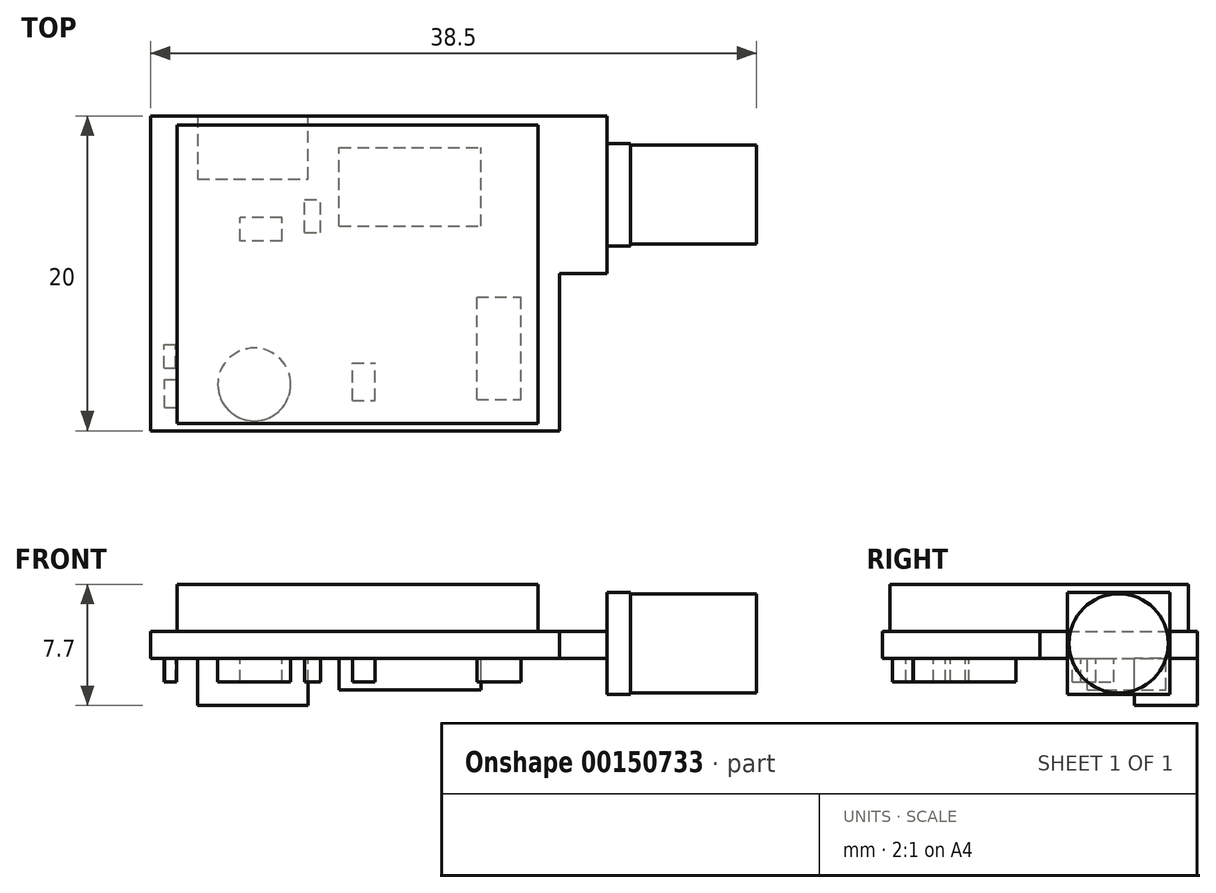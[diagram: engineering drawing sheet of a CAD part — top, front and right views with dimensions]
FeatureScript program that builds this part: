
annotation { "Feature Type Name" : "Feature", "Feature Type Description" : "" }
export const myFeature = defineFeature(function(context is Context, id is Id, definition is map)
    precondition{}
    {
        {
            var Q0;
            Q0=qCreatedBy(makeId("Top.planeOp"),FACE);
            var sketch = newSketch(context, id + "F0", { "sketchPlane" : qUnion([Q0])});
            skLineSegment(sketch, "E0.top", {"start": v(-26, 0) * mm, "end": v(0, 0) * mm});
            skLineSegment(sketch, "E0.left", {"start": v(-26, 20) * mm, "end": v(-26, 0) * mm});
            skLineSegment(sketch, "E1", {"start": v(0, 10) * mm, "end": v(3, 10) * mm});
            skLineSegment(sketch, "E2", {"start": v(3, 10) * mm, "end": v(3, 20) * mm});
            skLineSegment(sketch, "E3", {"start": v(0, 0) * mm, "end": v(0, 10) * mm});
            skLineSegment(sketch, "E4", {"start": v(3, 20) * mm, "end": v(-26, 20) * mm});
            skSolve(sketch);
        }
        {
            var Q0;
            Q0=makeQuery(id+"F0.imprint","IMPRINT",FACE,{"disambiguationData":[TD([[makeQuery(id+"F0.imprint","IMPRINT",EDGE,{"derivedFrom":sQuery(id+"F0.wireOp",EDGE,"E0.top")}),1.0]])]});
            extrude(context, id + "F1", {"entities" : qUnion([Q0]), "depth" : 1.7 * mm});
        }
        {
            var Q0;
            Q0=makeQuery(id+"F1.opExtrude","CAP_FACE",FACE,{"disambiguationData":[OSD([sQuery(id+"F0.wireOp",EDGE,"E0.top"),sQuery(id+"F0.wireOp",EDGE,"E0.left"),sQuery(id+"F0.wireOp",EDGE,"E1"),sQuery(id+"F0.wireOp",EDGE,"E2"),sQuery(id+"F0.wireOp",EDGE,"E3"),sQuery(id+"F0.wireOp",EDGE,"E4")])],"isStart":false});
            var sketch = newSketch(context, id + "F2", { "sketchPlane" : qUnion([Q0])});
            skLineSegment(sketch, "E5.bottom", {"start": v(-24.3, 19.42) * mm, "end": v(-1.39, 19.42) * mm});
            skLineSegment(sketch, "E5.top", {"start": v(-24.3, 0.48) * mm, "end": v(-1.39, 0.48) * mm});
            skLineSegment(sketch, "E5.left", {"start": v(-24.3, 19.42) * mm, "end": v(-24.3, 0.48) * mm});
            skLineSegment(sketch, "E5.right", {"start": v(-1.39, 19.42) * mm, "end": v(-1.39, 0.48) * mm});
            skSolve(sketch);
        }
        {
            var Q0;
            Q0=makeQuery(id+"F2.imprint","IMPRINT",FACE,{"disambiguationData":[TD([[makeQuery(id+"F2.imprint","IMPRINT",EDGE,{"derivedFrom":sQuery(id+"F2.wireOp",EDGE,"E5.bottom")}),-1.0]])]});
            extrude(context, id + "F3", {"entities" : qUnion([Q0]), "operationType" : NewBodyOperationType.ADD, "depth" : 3 * mm});
        }
        {
            var Q0;
            Q0=makeQuery(id+"F1.opExtrude","CAP_FACE",FACE,{"disambiguationData":[OSD([sQuery(id+"F0.wireOp",EDGE,"E0.top"),sQuery(id+"F0.wireOp",EDGE,"E0.left"),sQuery(id+"F0.wireOp",EDGE,"E1"),sQuery(id+"F0.wireOp",EDGE,"E2"),sQuery(id+"F0.wireOp",EDGE,"E3"),sQuery(id+"F0.wireOp",EDGE,"E4")])],"isStart":true});
            var sketch = newSketch(context, id + "F4", { "sketchPlane" : qUnion([Q0])});
            skLineSegment(sketch, "E6.bottom", {"start": v(-14, -13) * mm, "end": v(-5, -13) * mm});
            skLineSegment(sketch, "E6.top", {"start": v(-14, -18) * mm, "end": v(-5, -18) * mm});
            skLineSegment(sketch, "E6.left", {"start": v(-14, -13) * mm, "end": v(-14, -18) * mm});
            skLineSegment(sketch, "E6.right", {"start": v(-5, -13) * mm, "end": v(-5, -18) * mm});
            skSolve(sketch);
        }
        {
            var Q0;
            Q0=makeQuery(id+"F4.imprint","IMPRINT",FACE,{"disambiguationData":[TD([[makeQuery(id+"F4.imprint","IMPRINT",EDGE,{"derivedFrom":sQuery(id+"F4.wireOp",EDGE,"E6.bottom")}),-1.0]])]});
            extrude(context, id + "F5", {"entities" : qUnion([Q0]), "operationType" : NewBodyOperationType.ADD, "depth" : 2 * mm});
        }
        {
            var Q0;
            Q0=makeQuery(id+"F1.opExtrude","CAP_FACE",FACE,{"disambiguationData":[OSD([sQuery(id+"F0.wireOp",EDGE,"E0.top"),sQuery(id+"F0.wireOp",EDGE,"E0.left"),sQuery(id+"F0.wireOp",EDGE,"E1"),sQuery(id+"F0.wireOp",EDGE,"E2"),sQuery(id+"F0.wireOp",EDGE,"E3"),sQuery(id+"F0.wireOp",EDGE,"E4")])],"isStart":true});
            var sketch = newSketch(context, id + "F6", { "sketchPlane" : qUnion([Q0])});
            skLineSegment(sketch, "E7.bottom", {"start": v(-5.27, -1.98) * mm, "end": v(-2.46, -1.98) * mm});
            skLineSegment(sketch, "E7.top", {"start": v(-5.27, -8.48) * mm, "end": v(-2.46, -8.48) * mm});
            skLineSegment(sketch, "E7.left", {"start": v(-5.27, -1.98) * mm, "end": v(-5.27, -8.48) * mm});
            skLineSegment(sketch, "E7.right", {"start": v(-2.46, -1.98) * mm, "end": v(-2.46, -8.48) * mm});
            skLineSegment(sketch, "E8.bottom", {"start": v(-16.2, -12.6) * mm, "end": v(-15.2, -12.6) * mm});
            skLineSegment(sketch, "E8.top", {"start": v(-16.2, -14.68) * mm, "end": v(-15.2, -14.68) * mm});
            skLineSegment(sketch, "E8.left", {"start": v(-16.2, -12.6) * mm, "end": v(-16.2, -14.68) * mm});
            skLineSegment(sketch, "E8.right", {"start": v(-15.2, -12.6) * mm, "end": v(-15.2, -14.68) * mm});
            skLineSegment(sketch, "E9.bottom", {"start": v(-17.65, -12.06) * mm, "end": v(-20.3, -12.06) * mm});
            skLineSegment(sketch, "E9.top", {"start": v(-17.65, -13.54) * mm, "end": v(-20.3, -13.54) * mm});
            skLineSegment(sketch, "E9.left", {"start": v(-17.65, -12.06) * mm, "end": v(-17.65, -13.54) * mm});
            skLineSegment(sketch, "E9.right", {"start": v(-20.3, -12.06) * mm, "end": v(-20.3, -13.54) * mm});
            skLineSegment(sketch, "E10.bottom", {"start": v(-13.16, -1.93) * mm, "end": v(-11.72, -1.93) * mm});
            skLineSegment(sketch, "E10.top", {"start": v(-13.16, -4.32) * mm, "end": v(-11.72, -4.32) * mm});
            skLineSegment(sketch, "E10.left", {"start": v(-13.16, -1.93) * mm, "end": v(-13.16, -4.32) * mm});
            skLineSegment(sketch, "E10.right", {"start": v(-11.72, -1.93) * mm, "end": v(-11.72, -4.32) * mm});
            skLineSegment(sketch, "E11.bottom", {"start": v(-25.08, -1.5) * mm, "end": v(-24.34, -1.5) * mm});
            skLineSegment(sketch, "E11.top", {"start": v(-25.08, -3.25) * mm, "end": v(-24.34, -3.25) * mm});
            skLineSegment(sketch, "E11.left", {"start": v(-25.08, -1.5) * mm, "end": v(-25.08, -3.25) * mm});
            skLineSegment(sketch, "E11.right", {"start": v(-24.34, -1.5) * mm, "end": v(-24.34, -3.25) * mm});
            skLineSegment(sketch, "E12.bottom", {"start": v(-25.14, -4) * mm, "end": v(-24.4, -4) * mm});
            skLineSegment(sketch, "E12.top", {"start": v(-25.14, -5.5) * mm, "end": v(-24.4, -5.5) * mm});
            skLineSegment(sketch, "E12.left", {"start": v(-25.14, -4) * mm, "end": v(-25.14, -5.5) * mm});
            skLineSegment(sketch, "E12.right", {"start": v(-24.4, -4) * mm, "end": v(-24.4, -5.5) * mm});
            skCircle(sketch, "E13", {"center": v(-19.4, -2.94) * mm, "radius": 2.31 * mm});
            skSolve(sketch);
        }
        {
            var Q0;
            Q0 = qSketchRegion(id + "F6", true);
            extrude(context, id + "F7", {"entities" : qUnion([Q0]), "operationType" : NewBodyOperationType.ADD, "depth" : 1.5 * mm});
        }
        {
            var Q0;
            Q0=makeQuery(id+"F1.opExtrude","CAP_FACE",FACE,{"disambiguationData":[OSD([sQuery(id+"F0.wireOp",EDGE,"E0.top"),sQuery(id+"F0.wireOp",EDGE,"E0.left"),sQuery(id+"F0.wireOp",EDGE,"E1"),sQuery(id+"F0.wireOp",EDGE,"E2"),sQuery(id+"F0.wireOp",EDGE,"E3"),sQuery(id+"F0.wireOp",EDGE,"E4")])],"isStart":true});
            var sketch = newSketch(context, id + "F8", { "sketchPlane" : qUnion([Q0])});
            skLineSegment(sketch, "E14", {"start": v(-23, -20) * mm, "end": v(-23, -16) * mm});
            skLineSegment(sketch, "E15", {"start": v(-23, -16) * mm, "end": v(-16, -16) * mm});
            skLineSegment(sketch, "E16", {"start": v(-16, -16) * mm, "end": v(-16, -20) * mm});
            skSolve(sketch);
        }
        {
            var Q0;
            {var subQ0=sQuery(id+"F8.wireOp",EDGE,"E14");Q0=makeQuery(id+"F8.imprint","IMPRINT",FACE,{"disambiguationData":[TD([[makeQuery(id+"F8.imprint","IMPRINT",EDGE,{"derivedFrom":subQ0}),-1.0]])]});}
            extrude(context, id + "F9", {"entities" : qUnion([Q0]), "operationType" : NewBodyOperationType.ADD, "depth" : 3 * mm});
        }
        {
            var Q0;
            Q0=makeQuery(id+"F1.opExtrude","SWEPT_FACE",FACE,{"disambiguationData":[OSD([sQuery(id+"F0.wireOp",EDGE,"E2")])]});
            var sketch = newSketch(context, id + "F10", { "sketchPlane" : qUnion([Q0])});
            skLineSegment(sketch, "E17.bottom", {"start": v(18.25, -2.3) * mm, "end": v(11.75, -2.3) * mm});
            skLineSegment(sketch, "E17.top", {"start": v(18.25, 4.2) * mm, "end": v(11.75, 4.2) * mm});
            skLineSegment(sketch, "E17.left", {"start": v(18.25, -2.3) * mm, "end": v(18.25, 4.2) * mm});
            skLineSegment(sketch, "E17.right", {"start": v(11.75, -2.3) * mm, "end": v(11.75, 4.2) * mm});
            skSolve(sketch);
        }
        {
            var Q0;
            {var subQ0=sQuery(id+"F10.wireOp",EDGE,"E17.bottom");Q0=makeQuery(id+"F10.imprint","IMPRINT",FACE,{"disambiguationData":[TD([[makeQuery(id+"F10.imprint","IMPRINT",EDGE,{"derivedFrom":subQ0}),-1.0]])]});}
            var Q1;
            {var subQ0=sQuery(id+"F10.wireOp",EDGE,"E17.left");var subQ1=sQuery(id+"F0.wireOp",EDGE,"E2");var subQ2=makeQuery(id+"F1.opExtrude","CAP_EDGE",EDGE,{"disambiguationData":[OSD([subQ1])],"isStart":true});var subQ3=makeQuery(id+"F10.imprint","INTERSECT",VERTEX,{"derivedFrom":[subQ2,subQ0]});Q1=makeQuery(id+"F10.imprint","IMPRINT",FACE,{"disambiguationData":[TD([[makeQuery(id+"F10.imprint","IMPRINT",EDGE,{"disambiguationData":[TD([[subQ3,-1.0]])],"derivedFrom":subQ0}),1.0]])]});}
            var Q2;
            {var subQ0=sQuery(id+"F10.wireOp",EDGE,"E17.top");Q2=makeQuery(id+"F10.imprint","IMPRINT",FACE,{"disambiguationData":[TD([[makeQuery(id+"F10.imprint","IMPRINT",EDGE,{"derivedFrom":subQ0}),1.0]])]});}
            extrude(context, id + "F11", {"entities" : qUnion([Q0, Q1, Q2]), "operationType" : NewBodyOperationType.ADD, "depth" : 1.5 * mm});
        }
        {
            var Q0;
            Q0=makeQuery(id+"F11.opExtrude","CAP_FACE",FACE,{"disambiguationData":[OSD([sQuery(id+"F10.wireOp",EDGE,"E17.bottom"),sQuery(id+"F10.wireOp",EDGE,"E17.top"),sQuery(id+"F10.wireOp",EDGE,"E17.left"),sQuery(id+"F10.wireOp",EDGE,"E17.right")])],"isStart":false});
            var sketch = newSketch(context, id + "F12", { "sketchPlane" : qUnion([Q0])});
            skCircle(sketch, "E18", {"center": v(15, 0.95) * mm, "radius": 3.15 * mm});
            skPoint(sketch, "E18.centerSnap0", {"position": v(15, -2.3) * mm});
            skPoint(sketch, "E18.centerSnap1", {"position": v(18.25, 0.95) * mm});
            skSolve(sketch);
        }
        {
            var Q0;
            Q0=makeQuery(id+"F12.imprint","IMPRINT",FACE,{"disambiguationData":[TD([[makeQuery(id+"F12.imprint","IMPRINT",EDGE,{"derivedFrom":sQuery(id+"F12.wireOp",EDGE,"E18")}),1.0]])]});
            extrude(context, id + "F13", {"entities" : qUnion([Q0]), "operationType" : NewBodyOperationType.ADD, "depth" : 8 * mm});
        }
    });
